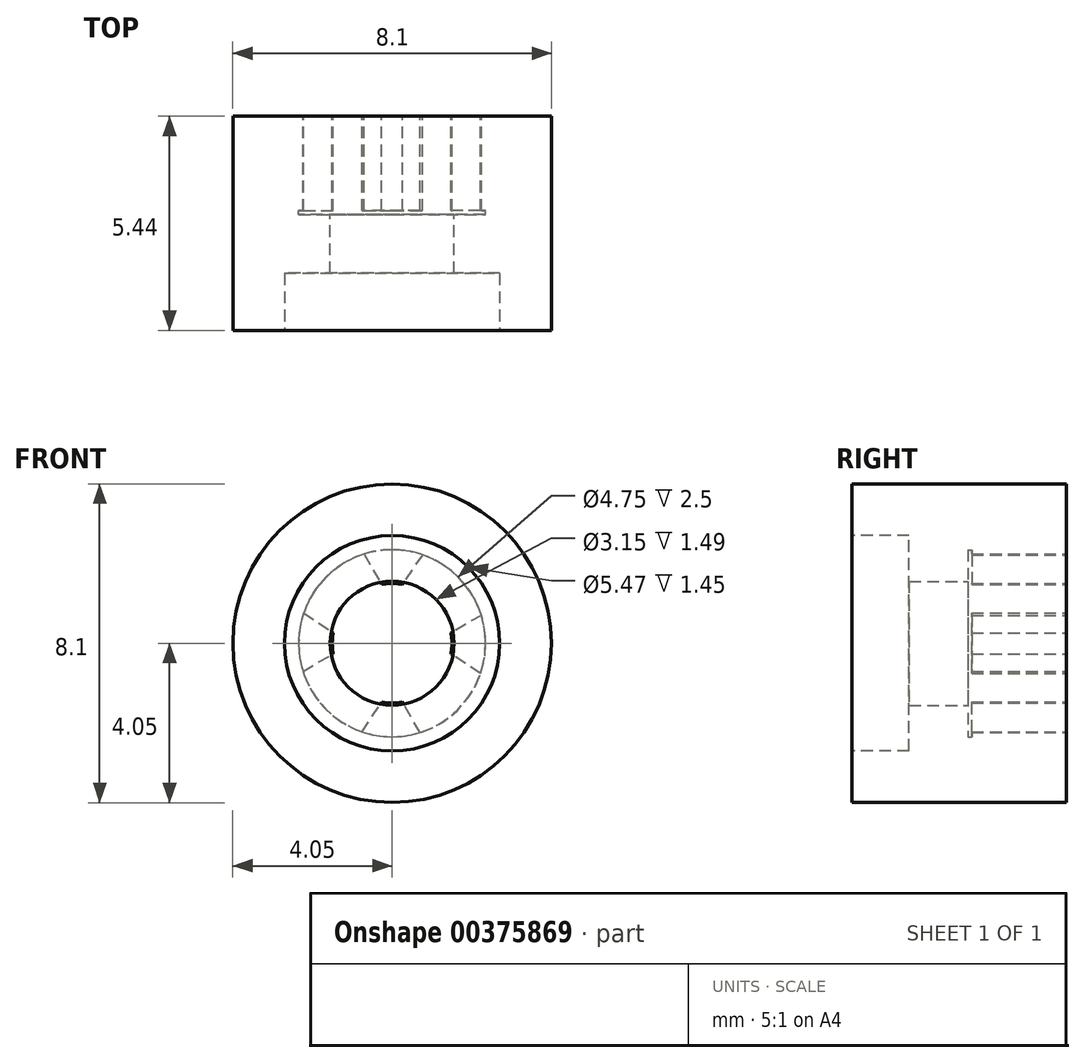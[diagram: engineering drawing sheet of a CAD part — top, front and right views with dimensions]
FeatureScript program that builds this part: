
annotation { "Feature Type Name" : "Feature", "Feature Type Description" : "" }
export const myFeature = defineFeature(function(context is Context, id is Id, definition is map)
    precondition{}
    {
        {
            var Q0;
            Q0=qCreatedBy(makeId("Front.planeOp"),FACE);
            var sketch = newSketch(context, id + "F0", { "sketchPlane" : qUnion([Q0])});
            skCircle(sketch, "E0", {"center": v(0, 0) * mm, "radius": 4.04 * mm});
            skCircle(sketch, "E1", {"center": v(0, 0) * mm, "radius": 1.57 * mm});
            skSolve(sketch);
        }
        {
            var Q0;
            Q0 = qSketchRegion(id + "F0", true);
            extrude(context, id + "F1", {"entities" : qUnion([Q0]), "depth" : 5.44 * mm});
        }
        {
            var Q0;
            Q0=makeQuery(id+"F1.opExtrude","CAP_FACE",FACE,{"disambiguationData":[OSD([sQuery(id+"F0.wireOp",EDGE,"E0"),sQuery(id+"F0.wireOp",EDGE,"E1")])],"isStart":false});
            var sketch = newSketch(context, id + "F2", { "sketchPlane" : qUnion([Q0])});
            skCircle(sketch, "E2", {"center": v(0, 0) * mm, "radius": 2.73 * mm});
            skSolve(sketch);
        }
        {
            var Q0;
            Q0 = qSketchRegion(id + "F2", true);
            extrude(context, id + "F3", {"entities" : qUnion([Q0]), "operationType" : NewBodyOperationType.REMOVE, "oppositeDirection" : true, "depth" : 1.45 * mm});
        }
        {
            var Q0;
            Q0=makeQuery(id+"F1.opExtrude","CAP_FACE",FACE,{"disambiguationData":[OSD([sQuery(id+"F0.wireOp",EDGE,"E0"),sQuery(id+"F0.wireOp",EDGE,"E1")])],"isStart":true});
            var sketch = newSketch(context, id + "F4", { "sketchPlane" : qUnion([Q0])});
            skCircle(sketch, "E3", {"center": v(0, 0) * mm, "radius": 2.38 * mm});
            skSolve(sketch);
        }
        {
            var Q0;
            Q0 = qSketchRegion(id + "F4", true);
            extrude(context, id + "F5", {"entities" : qUnion([Q0]), "operationType" : NewBodyOperationType.REMOVE, "oppositeDirection" : true, "depth" : 2.5 * mm});
        }
        {
            var Q0;
            Q0=makeQuery(id+"F1.opExtrude","CAP_FACE",FACE,{"disambiguationData":[OSD([sQuery(id+"F0.wireOp",EDGE,"E0"),sQuery(id+"F0.wireOp",EDGE,"E1")])],"isStart":true});
            var sketch = newSketch(context, id + "F6", { "sketchPlane" : qUnion([Q0])});
            skLineSegment(sketch, "E4", {"start": v(0.77, -2.25) * mm, "end": v(0.27, -1.5) * mm});
            skLineSegment(sketch, "E5", {"start": v(-0.7, -2.27) * mm, "end": v(-0.27, -1.5) * mm});
            skArc(sketch, "E6", {"start": v(-0.27, -1.5) * mm, "mid": v(0, -1.52) * mm, "end": v(0.27, -1.5) * mm});
            skLineSegment(sketch, "E7.1.0", {"start": v(2.25, 0.77) * mm, "end": v(1.5, 0.27) * mm});
            skArc(sketch, "E7.1.1", {"start": v(1.5, -0.27) * mm, "mid": v(1.52, 0) * mm, "end": v(1.5, 0.27) * mm});
            skLineSegment(sketch, "E7.1.2", {"start": v(2.27, -0.7) * mm, "end": v(1.5, -0.27) * mm});
            skLineSegment(sketch, "E7.2.0", {"start": v(-0.77, 2.25) * mm, "end": v(-0.27, 1.5) * mm});
            skArc(sketch, "E7.2.1", {"start": v(0.27, 1.5) * mm, "mid": v(0, 1.52) * mm, "end": v(-0.27, 1.5) * mm});
            skLineSegment(sketch, "E7.2.2", {"start": v(0.7, 2.27) * mm, "end": v(0.27, 1.5) * mm});
            skLineSegment(sketch, "E7.3.0", {"start": v(-2.25, -0.77) * mm, "end": v(-1.5, -0.27) * mm});
            skArc(sketch, "E7.3.1", {"start": v(-1.5, 0.27) * mm, "mid": v(-1.52, 0) * mm, "end": v(-1.5, -0.27) * mm});
            skLineSegment(sketch, "E7.3.2", {"start": v(-2.27, 0.7) * mm, "end": v(-1.5, 0.27) * mm});
            skSolve(sketch);
        }
        {
            var Q0;
            {var subQ0=sQuery(id+"F6.wireOp",EDGE,"E7.1.0");Q0=makeQuery(id+"F6.imprint","IMPRINT",FACE,{"disambiguationData":[TD([[makeQuery(id+"F6.imprint","IMPRINT",EDGE,{"derivedFrom":subQ0}),1.0]])]});}
            var Q1;
            {var subQ0=sQuery(id+"F6.wireOp",EDGE,"E4");Q1=makeQuery(id+"F6.imprint","IMPRINT",FACE,{"disambiguationData":[TD([[makeQuery(id+"F6.imprint","IMPRINT",EDGE,{"derivedFrom":subQ0}),1.0]])]});}
            var Q2;
            {var subQ0=sQuery(id+"F6.wireOp",EDGE,"E7.3.0");Q2=makeQuery(id+"F6.imprint","IMPRINT",FACE,{"disambiguationData":[TD([[makeQuery(id+"F6.imprint","IMPRINT",EDGE,{"derivedFrom":subQ0}),1.0]])]});}
            var Q3;
            {var subQ0=sQuery(id+"F6.wireOp",EDGE,"E7.2.0");Q3=makeQuery(id+"F6.imprint","IMPRINT",FACE,{"disambiguationData":[TD([[makeQuery(id+"F6.imprint","IMPRINT",EDGE,{"derivedFrom":subQ0}),1.0]])]});}
            var Q4;
            Q4=sQuery(id+"F6.wireOp",EDGE,"E6");
            var Q5;
            Q5=sQuery(id+"F6.wireOp",EDGE,"E4");
            var Q6;
            Q6=sQuery(id+"F6.wireOp",EDGE,"E5");
            var Q7;
            Q7=sQuery(id+"F6.wireOp",EDGE,"E7.3.0");
            var Q8;
            Q8=sQuery(id+"F6.wireOp",EDGE,"E7.3.1");
            var Q9;
            Q9=sQuery(id+"F6.wireOp",EDGE,"E7.3.2");
            var Q10;
            Q10=sQuery(id+"F6.wireOp",EDGE,"E7.2.0");
            var Q11;
            Q11=sQuery(id+"F6.wireOp",EDGE,"E7.2.1");
            var Q12;
            Q12=sQuery(id+"F6.wireOp",EDGE,"E7.2.2");
            var Q13;
            Q13=sQuery(id+"F6.wireOp",EDGE,"E7.1.0");
            var Q14;
            Q14=sQuery(id+"F6.wireOp",EDGE,"E7.1.1");
            var Q15;
            Q15=sQuery(id+"F6.wireOp",EDGE,"E7.1.2");
            extrude(context, id + "F7", {"entities" : qUnion([Q0, Q1, Q2, Q3]), "operationType" : NewBodyOperationType.ADD, "surfaceEntities" : qUnion([Q4, Q5, Q6, Q7, Q8, Q9, Q10, Q11, Q12, Q13, Q14, Q15]), "oppositeDirection" : true, "depth" : 2.4 * mm});
        }
    });
